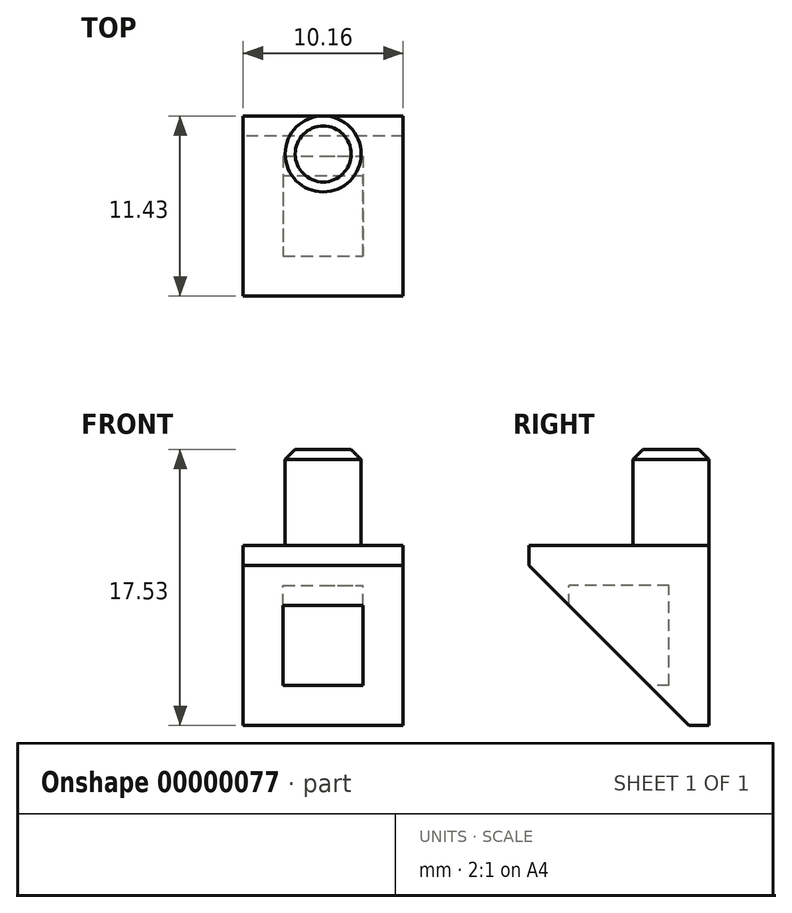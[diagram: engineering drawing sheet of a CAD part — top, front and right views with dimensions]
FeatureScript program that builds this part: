
annotation { "Feature Type Name" : "Feature", "Feature Type Description" : "" }
export const myFeature = defineFeature(function(context is Context, id is Id, definition is map)
    precondition{}
    {
        {
            var Q0;
            Q0=qCreatedBy(makeId("Top.planeOp"),FACE);
            var sketch = newSketch(context, id + "F0", { "sketchPlane" : qUnion([Q0])});
            skCircle(sketch, "E0", {"center": v(0, 0) * mm, "radius": 2.41 * mm});
            skLineSegment(sketch, "E1.bottom", {"start": v(-5.08, 2.41) * mm, "end": v(5.08, 2.41) * mm});
            skLineSegment(sketch, "E1.top", {"start": v(-5.08, -9.02) * mm, "end": v(5.08, -9.02) * mm});
            skLineSegment(sketch, "E1.left", {"start": v(-5.08, 2.41) * mm, "end": v(-5.08, -9.02) * mm});
            skLineSegment(sketch, "E1.right", {"start": v(5.08, 2.41) * mm, "end": v(5.08, -9.02) * mm});
            skPoint(sketch, "E2", {"position": v(0, 2.41) * mm});
            skSolve(sketch);
        }
        {
            var Q0;
            Q0=makeQuery(id+"F0.imprint","IMPRINT",FACE,{"disambiguationData":[TD([[makeQuery(id+"F0.imprint","IMPRINT",EDGE,{"derivedFrom":sQuery(id+"F0.wireOp",EDGE,"E0")}),1.0]])]});
            extrude(context, id + "F1", {"entities" : qUnion([Q0]), "depth" : 6.1 * mm});
        }
        {
            var Q0;
            {var subQ3=sQuery(id+"F0.wireOp",EDGE,"E0");Q0=makeQuery(id+"F0.imprint","IMPRINT",FACE,{"disambiguationData":[TD([[makeQuery(id+"F0.imprint","IMPRINT",EDGE,{"derivedFrom":subQ3}),-1.0]])]});}
            var Q1;
            Q1=makeQuery(id+"F0.imprint","IMPRINT",FACE,{"disambiguationData":[TD([[makeQuery(id+"F0.imprint","IMPRINT",EDGE,{"derivedFrom":sQuery(id+"F0.wireOp",EDGE,"E0")}),1.0]])]});
            extrude(context, id + "F2", {"entities" : qUnion([Q0, Q1]), "operationType" : NewBodyOperationType.ADD, "oppositeDirection" : true, "depth" : 11.43 * mm});
        }
        {
            var Q0;
            Q0=makeQuery(id+"F2.opExtrude","CAP_EDGE",EDGE,{"disambiguationData":[OSD([sQuery(id+"F0.wireOp",EDGE,"E1.top")])],"isStart":false});
            chamfer(context, id + "F3", {"entities" : qUnion([Q0]), "width" : 10.16 * mm, "tangentPropagation" : true});
        }
        {
            var Q0;
            Q0=makeQuery(id+"F3.opChamfer","BLEND_FACE",FACE,{"disambiguationData":[OSD([sQuery(id+"F0.wireOp",EDGE,"E1.top")])]});
            shell(context, id + "F4", {"entities" : qUnion([Q0]), "thickness" : 2.54 * mm});
        }
        {
            var Q0;
            Q0=makeQuery(id+"F1.opExtrude","CAP_EDGE",EDGE,{"disambiguationData":[OSD([sQuery(id+"F0.wireOp",EDGE,"E0")])],"isStart":false});
            chamfer(context, id + "F5", {"entities" : qUnion([Q0]), "width" : 0.64 * mm, "tangentPropagation" : true});
        }
    });
